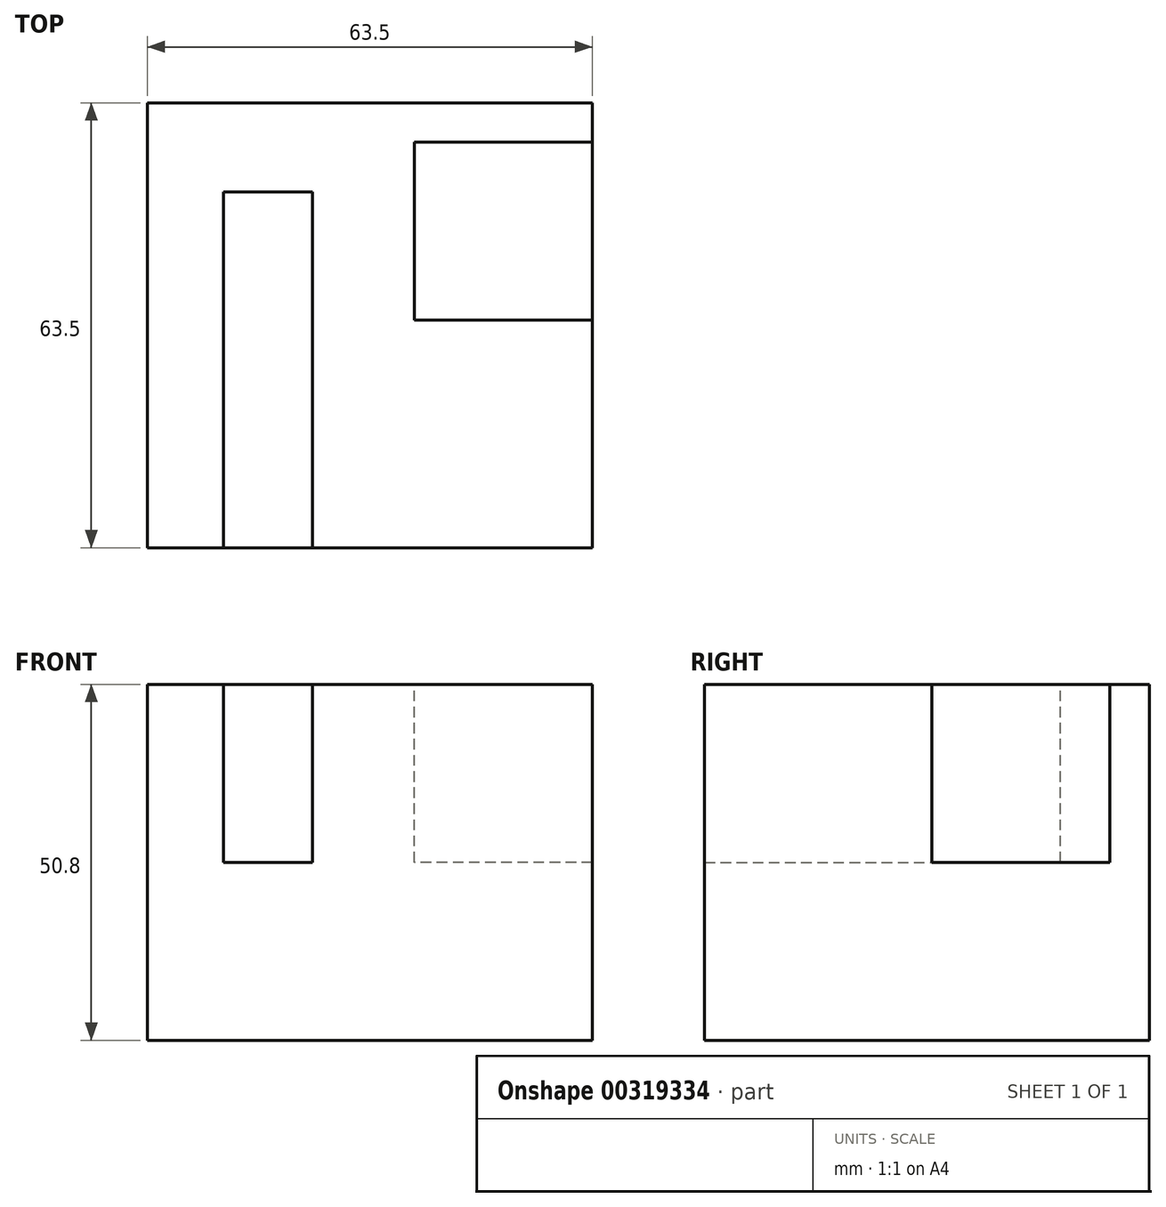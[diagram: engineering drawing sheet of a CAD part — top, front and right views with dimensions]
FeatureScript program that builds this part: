
annotation { "Feature Type Name" : "Feature", "Feature Type Description" : "" }
export const myFeature = defineFeature(function(context is Context, id is Id, definition is map)
    precondition{}
    {
        {
            var Q0;
            Q0=qCreatedBy(makeId("Top.planeOp"),FACE);
            var sketch = newSketch(context, id + "F0", { "sketchPlane" : qUnion([Q0])});
            skLineSegment(sketch, "E0.bottom", {"start": v(-25.92, 37.7) * mm, "end": v(37.58, 37.7) * mm});
            skLineSegment(sketch, "E0.top", {"start": v(-25.92, -25.8) * mm, "end": v(37.58, -25.8) * mm});
            skLineSegment(sketch, "E0.left", {"start": v(-25.92, 37.7) * mm, "end": v(-25.92, -25.8) * mm});
            skLineSegment(sketch, "E0.right", {"start": v(37.58, 37.7) * mm, "end": v(37.58, -25.8) * mm});
            skSolve(sketch);
        }
        {
            var Q0;
            Q0 = qSketchRegion(id + "F0", true);
            extrude(context, id + "F1", {"entities" : qUnion([Q0]), "depth" : 50.8 * mm});
        }
        {
            var Q0;
            Q0=makeQuery(id+"F1.opExtrude","CAP_FACE",FACE,{"disambiguationData":[OSD([sQuery(id+"F0.wireOp",EDGE,"E0.bottom"),sQuery(id+"F0.wireOp",EDGE,"E0.top"),sQuery(id+"F0.wireOp",EDGE,"E0.left"),sQuery(id+"F0.wireOp",EDGE,"E0.right")])],"isStart":false});
            var sketch = newSketch(context, id + "F2", { "sketchPlane" : qUnion([Q0])});
            skLineSegment(sketch, "E1", {"start": v(-15.05, -25.8) * mm, "end": v(-15.05, 25) * mm});
            skLineSegment(sketch, "E2", {"start": v(-15.05, 25) * mm, "end": v(-2.35, 25) * mm});
            skLineSegment(sketch, "E3", {"start": v(-2.35, 25) * mm, "end": v(-2.35, -25.8) * mm});
            skLineSegment(sketch, "E4", {"start": v(-2.35, -25.8) * mm, "end": v(-15.05, -25.8) * mm});
            skSolve(sketch);
        }
        {
            var Q0;
            Q0 = qSketchRegion(id + "F2", true);
            extrude(context, id + "F3", {"entities" : qUnion([Q0]), "operationType" : NewBodyOperationType.REMOVE, "oppositeDirection" : true, "depth" : 25.4 * mm});
        }
        {
            var Q0;
            Q0=makeQuery(id+"F1.opExtrude","CAP_FACE",FACE,{"disambiguationData":[OSD([sQuery(id+"F0.wireOp",EDGE,"E0.bottom"),sQuery(id+"F0.wireOp",EDGE,"E0.top"),sQuery(id+"F0.wireOp",EDGE,"E0.left"),sQuery(id+"F0.wireOp",EDGE,"E0.right")])],"isStart":false});
            var sketch = newSketch(context, id + "F4", { "sketchPlane" : qUnion([Q0])});
            skLineSegment(sketch, "E5", {"start": v(37.58, 32.08) * mm, "end": v(12.18, 32.08) * mm});
            skLineSegment(sketch, "E6", {"start": v(12.18, 32.08) * mm, "end": v(12.18, 6.68) * mm});
            skLineSegment(sketch, "E7", {"start": v(12.18, 6.68) * mm, "end": v(37.58, 6.68) * mm});
            skLineSegment(sketch, "E8", {"start": v(37.58, 6.68) * mm, "end": v(37.58, 32.08) * mm});
            skSolve(sketch);
        }
        {
            var Q0;
            Q0 = qSketchRegion(id + "F4", true);
            extrude(context, id + "F5", {"entities" : qUnion([Q0]), "operationType" : NewBodyOperationType.REMOVE, "oppositeDirection" : true, "depth" : 25.4 * mm});
        }
    });
